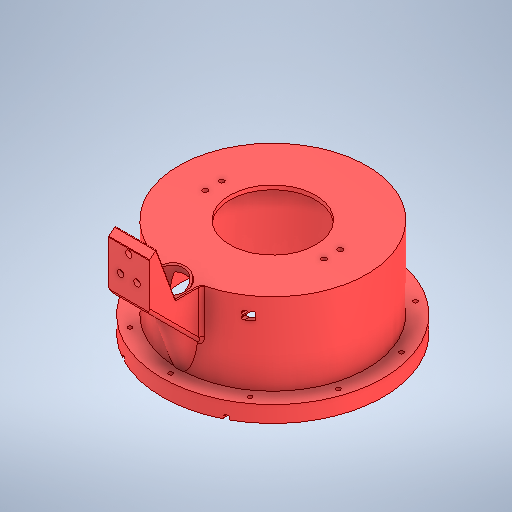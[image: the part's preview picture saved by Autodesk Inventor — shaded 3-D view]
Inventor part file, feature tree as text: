
AUTODESK INVENTOR PART (.ipt)
format: ipt  version: 2025 (Build 290162000, 162)  size: 1,082,368 bytes
history: native  units: in
note: dims shown in document units (in); Inventor stores cm internally (conversion verified against a paired STEP export)
features: emboss x1, sketch x1, other x1
ambient origin geometry x8: Origin, YZ Plane, XZ Plane, XY Plane, X Axis, Y Axis, Z Axis, Center Point
bodies: Solid1 (feature_tree)
feature tree (3):
  emboss  "Emboss1"
  sketch  "Sketch1"  dims[d0=0.0394in d1=0.0in]
  other  "top cyclinder"
